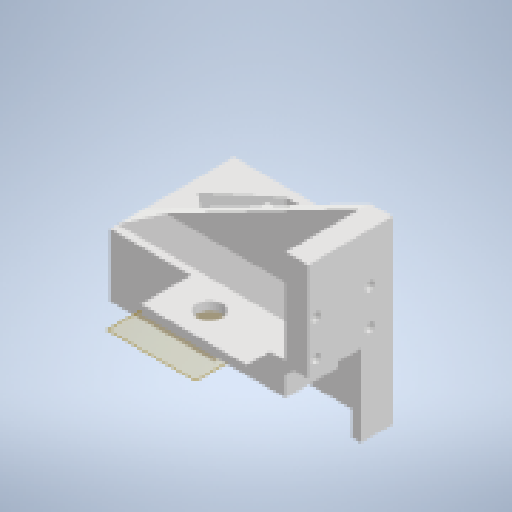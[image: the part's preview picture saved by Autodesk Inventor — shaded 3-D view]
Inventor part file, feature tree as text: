
AUTODESK INVENTOR PART (.ipt)
format: ipt  version: 2024.2 (Build 282272000, 272)  size: 348,672 bytes
history: native  units: mm
features: extrude x16, sketch x14, other x7, reference x6, chamfer x5, projected_geometry x3
ambient origin geometry x8: Origin, YZ Plane, XZ Plane, XY Plane, X Axis, Y Axis, Z Axis, Center Point
bodies: Body1 (feature_tree)
feature tree (51):
  other  "Твердое тело1"
  other  "РабПлоскость1"
  sketch  "Эскиз1"
  extrude  "Выдавливание1"  Depth=2.0mm TaperAngle=0.0deg
  extrude  "Выдавливание2"  Depth=1.5mm
  extrude  "Выдавливание3"  Depth=1.5mm
  extrude  "Выдавливание4"  Depth=12.0mm TaperAngle=0.0deg
  extrude  "Выдавливание5"  Depth=8.0mm TaperAngle=0.0deg
  extrude  "Выдавливание6"  Depth=12.0mm TaperAngle=0.0deg
  extrude  "Выдавливание7"  Depth=20.0mm
  sketch  "Эскиз6"
  extrude  "Выдавливание8"  Depth=18.0mm
  extrude  "Выдавливание9"  Depth=2.0mm
  sketch  "Эскиз7"
  other  "РабПлоскость2"
  extrude  "Выдавливание10"  Depth=18.9mm
  extrude  "Выдавливание11"  Depth=22.9mm
  extrude  "Выдавливание12"  Depth=3.0mm
  sketch  "Эскиз10"
  extrude  "Выдавливание13"  TaperAngle=0.0deg  [1 undecoded]
  extrude  "Выдавливание14"  Depth=4.2mm
  chamfer  "Фаска2"  [1 undecoded]
  chamfer  "Фаска3"  Distance=2.0mm
  chamfer  "Фаска4"  Distance=1.500103mm
  chamfer  "Фаска5"  Distance=19.2mm
  extrude  "Выдавливание15"  Depth=2.0mm TaperAngle=0.0deg
  extrude  "Выдавливание16"  Depth=2.0mm TaperAngle=0.0deg
  chamfer  "Фаска6"  Distance=3.0mm
  reference  "Ссылка1"
  reference  "Ссылка2"
  reference  "Ссылка3"
  sketch  "Эскиз2"
  sketch  "Эскиз3"
  sketch  "Эскиз4"
  sketch  "Эскиз5"
  reference  "Ссылка4"
  reference  "Ссылка5"
  projected_geometry  "Спроецированная петля1"
  sketch  "Эскиз8"
  sketch  "Эскиз9"
  reference  "Ссылка6"
  projected_geometry  "Спроецированная петля2"
  sketch  "Эскиз11"
  sketch  "Эскиз12"
  sketch  "Эскиз14"
  projected_geometry  "Спроецированная петля3"
  sketch  "Эскиз15"
  other  "<userpath>\Documents\Artist-v2\3D\каретка.iam"
  other  "каретка.iam"
  other  "крепежная основа:1"
  other  "Сервопривод:1"
note: 2 required parameter values undecoded (feature->parameter linkage not recoverable at this tier; creation-order binding heuristic only, values carry confidence <= 0.55)
